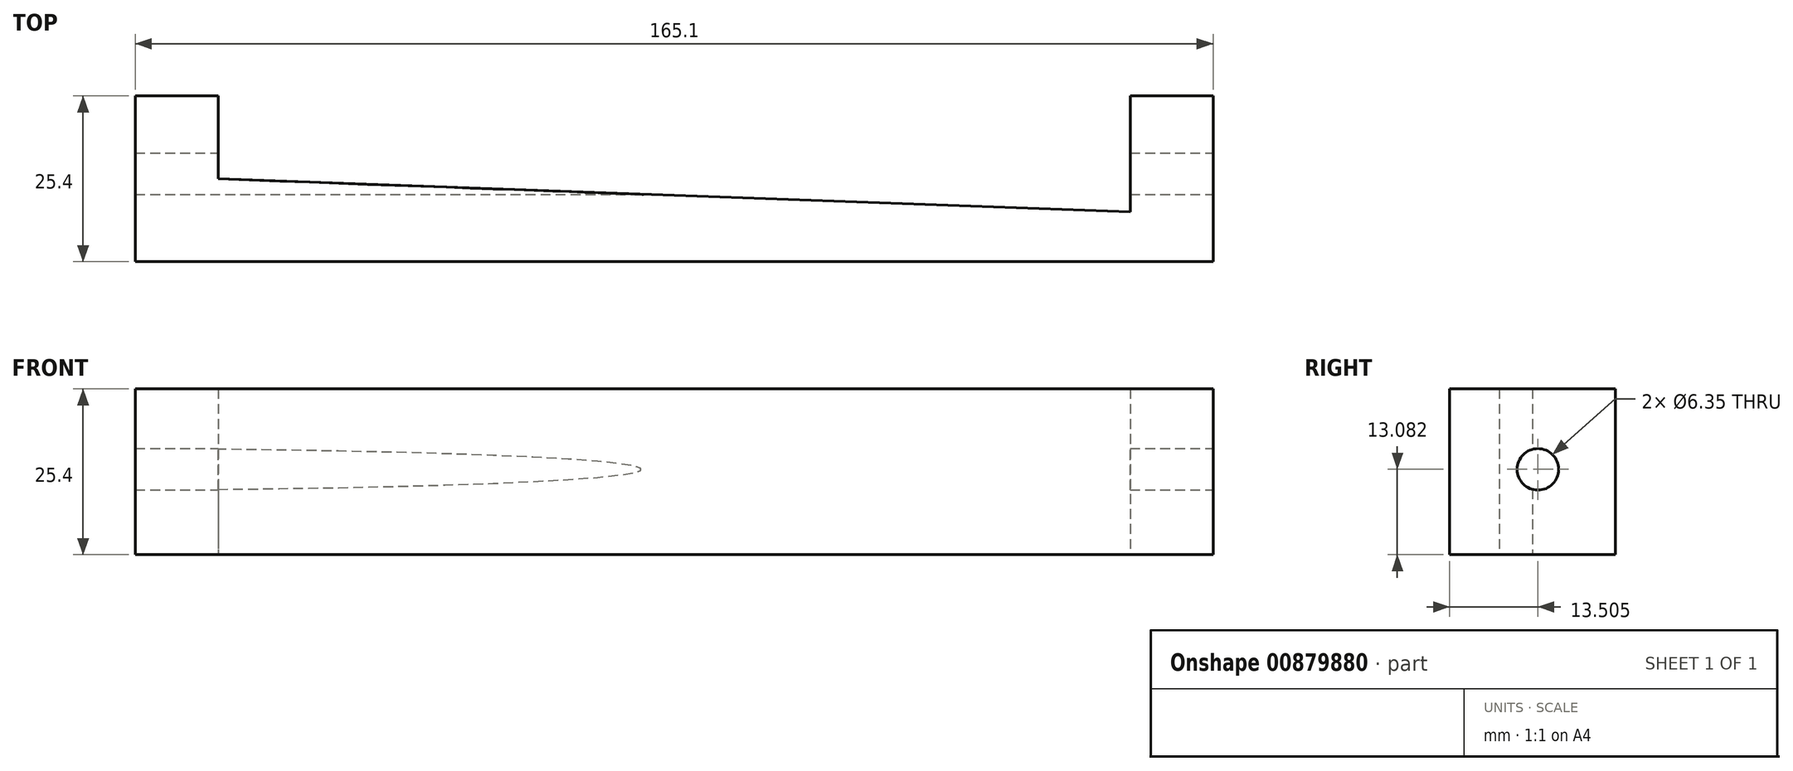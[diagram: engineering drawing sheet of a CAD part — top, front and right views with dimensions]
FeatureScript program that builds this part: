
annotation { "Feature Type Name" : "Feature", "Feature Type Description" : "" }
export const myFeature = defineFeature(function(context is Context, id is Id, definition is map)
    precondition{}
    {
        {
            var Q0;
            Q0=qCreatedBy(makeId("Top.planeOp"),FACE);
            var sketch = newSketch(context, id + "F0", { "sketchPlane" : qUnion([Q0])});
            skLineSegment(sketch, "E0", {"start": v(-106.88, 50.49) * mm, "end": v(-106.88, 25.09) * mm});
            skLineSegment(sketch, "E1", {"start": v(-106.88, 25.09) * mm, "end": v(58.22, 25.09) * mm});
            skLineSegment(sketch, "E2", {"start": v(58.22, 25.09) * mm, "end": v(58.22, 50.49) * mm});
            skLineSegment(sketch, "E3", {"start": v(58.22, 50.49) * mm, "end": v(45.52, 50.49) * mm});
            skLineSegment(sketch, "E4", {"start": v(-94.18, 50.49) * mm, "end": v(-106.88, 50.49) * mm});
            skLineSegment(sketch, "E5", {"start": v(-94.18, 50.49) * mm, "end": v(-94.18, 37.79) * mm});
            skLineSegment(sketch, "E6", {"start": v(45.52, 50.49) * mm, "end": v(45.52, 32.7) * mm});
            skLineSegment(sketch, "E7", {"start": v(45.52, 32.7) * mm, "end": v(-94.18, 37.79) * mm});
            skSolve(sketch);
        }
        {
            var Q0;
            Q0 = qSketchRegion(id + "F0", true);
            extrude(context, id + "F1", {"entities" : qUnion([Q0]), "depth" : 25.4 * mm, "offsetDistance" : 25.4 * mm});
        }
        {
            var Q0;
            Q0=makeQuery(id+"F1.opExtrude","SWEPT_FACE",FACE,{"disambiguationData":[OSD([sQuery(id+"F0.wireOp",EDGE,"E2")])]});
            var sketch = newSketch(context, id + "F2", { "sketchPlane" : qUnion([Q0])});
            skCircle(sketch, "E8", {"center": v(38.6, 13.08) * mm, "radius": 6.35 * mm});
            skSolve(sketch);
        }
        {
            var Q0;
            Q0=sQuery(id+"F2.wireOp",VERTEX,"E8.center");
            var Q1;
            Q1=makeQuery(id+"F1.opExtrude","SWEPT_BODY",BODY,{"disambiguationData":[OSD([sQuery(id+"F0.wireOp",EDGE,"E0"),sQuery(id+"F0.wireOp",EDGE,"E1"),sQuery(id+"F0.wireOp",EDGE,"E2"),sQuery(id+"F0.wireOp",EDGE,"E3"),sQuery(id+"F0.wireOp",EDGE,"E4"),sQuery(id+"F0.wireOp",EDGE,"E5"),sQuery(id+"F0.wireOp",EDGE,"E6"),sQuery(id+"F0.wireOp",EDGE,"E7")])]});
            hole(context, id + "F3", {"style" : HoleStyle.SIMPLE, "endStyle" : HoleEndStyle.THROUGH, "holeDiameter" : 6.35 * mm, "majorDiameter" : 6.35 * mm, "isTappedThrough" : true, "tappedDepth" : 12.7 * mm, "tapClearance" : 3, "locations" : qUnion([Q0]), "scope" : qUnion([Q1])});
        }
    });
